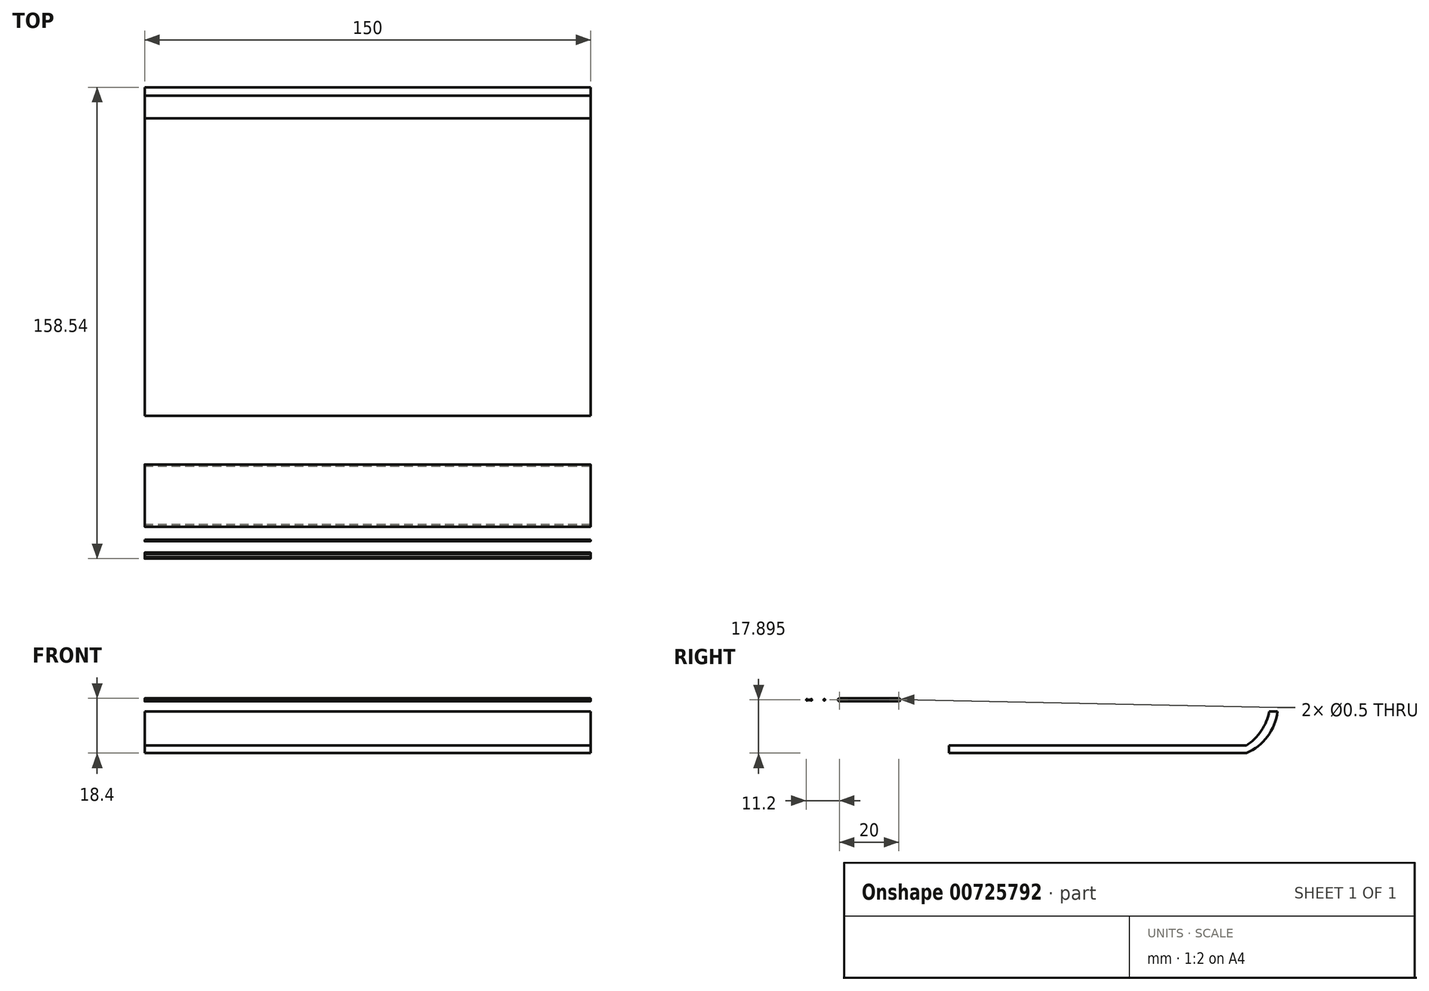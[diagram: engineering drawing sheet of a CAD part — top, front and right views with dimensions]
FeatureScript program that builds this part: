
annotation { "Feature Type Name" : "Feature", "Feature Type Description" : "" }
export const myFeature = defineFeature(function(context is Context, id is Id, definition is map)
    precondition{}
    {
        {
            var Q0;
            Q0=qCreatedBy(makeId("Right.planeOp"),FACE);
            var sketch = newSketch(context, id + "F0", { "sketchPlane" : qUnion([Q0])});
            skLineSegment(sketch, "E0", {"start": v(-20, 28.25) * mm, "end": v(0, 28.25) * mm});
            skArc(sketch, "E1", {"start": v(-20, 28.25) * mm, "mid": v(-20.5, 27.75) * mm, "end": v(-20, 27.25) * mm});
            skLineSegment(sketch, "E2", {"start": v(-20, 27.25) * mm, "end": v(0, 27.25) * mm});
            skCircle(sketch, "E3", {"center": v(-20, 27.75) * mm, "radius": 0.25 * mm});
            skCircle(sketch, "E4", {"center": v(-25.1, 27.75) * mm, "radius": 0.25 * mm});
            skArc(sketch, "E5", {"start": v(0, 27.25) * mm, "mid": v(0.5, 27.75) * mm, "end": v(0, 28.25) * mm});
            skPoint(sketch, "E5.centerSnap0", {"position": v(0, 27.75) * mm});
            skPoint(sketch, "E6.orphan", {"position": v(0, 28.25) * mm});
            skPoint(sketch, "E7.start.orphan", {"position": v(0, 27.25) * mm});
            skCircle(sketch, "E8", {"center": v(0, 27.75) * mm, "radius": 0.25 * mm});
            skLineSegment(sketch, "E9", {"start": v(16.86, 12.35) * mm, "end": v(116.86, 12.35) * mm});
            skLineSegment(sketch, "E10", {"start": v(16.86, 12.35) * mm, "end": v(16.86, 9.85) * mm});
            skLineSegment(sketch, "E11", {"start": v(16.86, 9.85) * mm, "end": v(116.86, 9.85) * mm});
            skArc(sketch, "E12", {"start": v(-29.63, 27.92) * mm, "mid": v(-29.66, 27.87) * mm, "end": v(-29.69, 27.8) * mm});
            skArc(sketch, "E13", {"start": v(-30.95, 28) * mm, "mid": v(-31.2, 27.73) * mm, "end": v(-30.92, 27.5) * mm});
            skLineSegment(sketch, "E14", {"start": v(-30.95, 28) * mm, "end": v(-30.95, 28) * mm});
            skLineSegment(sketch, "E15", {"start": v(-30.92, 27.5) * mm, "end": v(-30.92, 27.5) * mm});
            skLineSegment(sketch, "E16", {"start": v(-30.77, 27.92) * mm, "end": v(-30.77, 27.92) * mm});
            skLineSegment(sketch, "E17", {"start": v(-30.74, 27.61) * mm, "end": v(-30.74, 27.61) * mm});
            skArc(sketch, "E18.trimOffspring", {"start": v(-30.74, 27.61) * mm, "mid": v(-30.72, 27.66) * mm, "end": v(-30.7, 27.7) * mm});
            skArc(sketch, "E19.trimOffspring", {"start": v(-29.45, 27.5) * mm, "mid": v(-29.2, 27.75) * mm, "end": v(-29.45, 28) * mm});
            skArc(sketch, "E20", {"start": v(-30.71, 27.8) * mm, "mid": v(-31.2, 27.73) * mm, "end": v(-30.7, 27.7) * mm});
            skArc(sketch, "E21", {"start": v(-29.7, 27.7) * mm, "mid": v(-29.2, 27.73) * mm, "end": v(-29.69, 27.8) * mm});
            skLineSegment(sketch, "E22", {"start": v(-30.71, 27.8) * mm, "end": v(-29.69, 27.8) * mm});
            skLineSegment(sketch, "E23", {"start": v(-30.7, 27.7) * mm, "end": v(-29.7, 27.7) * mm});
            skArc(sketch, "E24.trimOffspring", {"start": v(-30.71, 27.8) * mm, "mid": v(-30.73, 27.87) * mm, "end": v(-30.77, 27.92) * mm});
            skArc(sketch, "E25.trimOffspring", {"start": v(-29.7, 27.7) * mm, "mid": v(-29.68, 27.65) * mm, "end": v(-29.66, 27.61) * mm});
            skArc(sketch, "E26", {"start": v(116.86, 12.35) * mm, "mid": v(121.9, 17.32) * mm, "end": v(124.58, 23.86) * mm});
            skArc(sketch, "E27", {"start": v(116.86, 9.85) * mm, "mid": v(124, 15.44) * mm, "end": v(127.34, 23.86) * mm});
            skLineSegment(sketch, "E28", {"start": v(124.58, 23.86) * mm, "end": v(127.34, 23.86) * mm});
            skSolve(sketch);
        }
        {
            var Q0;
            Q0=makeQuery(id+"F0.imprint","IMPRINT",FACE,{"disambiguationData":[TD([[makeQuery(id+"F0.imprint","IMPRINT",EDGE,{"derivedFrom":sQuery(id+"F0.wireOp",EDGE,"E0")}),-1.0]])]});
            extrude(context, id + "F1", {"entities" : qUnion([Q0]), "depth" : 150 * mm, "offsetDistance" : 25 * mm});
        }
        {
            var Q0;
            Q0=makeQuery(id+"F0.imprint","IMPRINT",FACE,{"disambiguationData":[TD([[makeQuery(id+"F0.imprint","IMPRINT",EDGE,{"derivedFrom":sQuery(id+"F0.wireOp",EDGE,"E4")}),1.0]])]});
            extrude(context, id + "F2", {"entities" : qUnion([Q0]), "depth" : 150 * mm, "offsetDistance" : 25 * mm});
        }
        {
            var Q0;
            Q0=makeQuery(id+"F0.imprint","IMPRINT",FACE,{"disambiguationData":[TD([[makeQuery(id+"F0.imprint","IMPRINT",EDGE,{"derivedFrom":sQuery(id+"F0.wireOp",EDGE,"E9")}),-1.0]])]});
            extrude(context, id + "F3", {"entities" : qUnion([Q0]), "depth" : 150 * mm, "offsetDistance" : 25 * mm});
        }
        {
            var Q0;
            {var subQ1=sQuery(id+"F0.wireOp",EDGE,"E22");Q0=makeQuery(id+"F0.imprint","IMPRINT",FACE,{"disambiguationData":[TD([[makeQuery(id+"F0.imprint","IMPRINT",EDGE,{"derivedFrom":subQ1}),-1.0]])]});}
            extrude(context, id + "F4", {"entities" : qUnion([Q0]), "depth" : 150 * mm, "offsetDistance" : 25 * mm});
        }
    });
